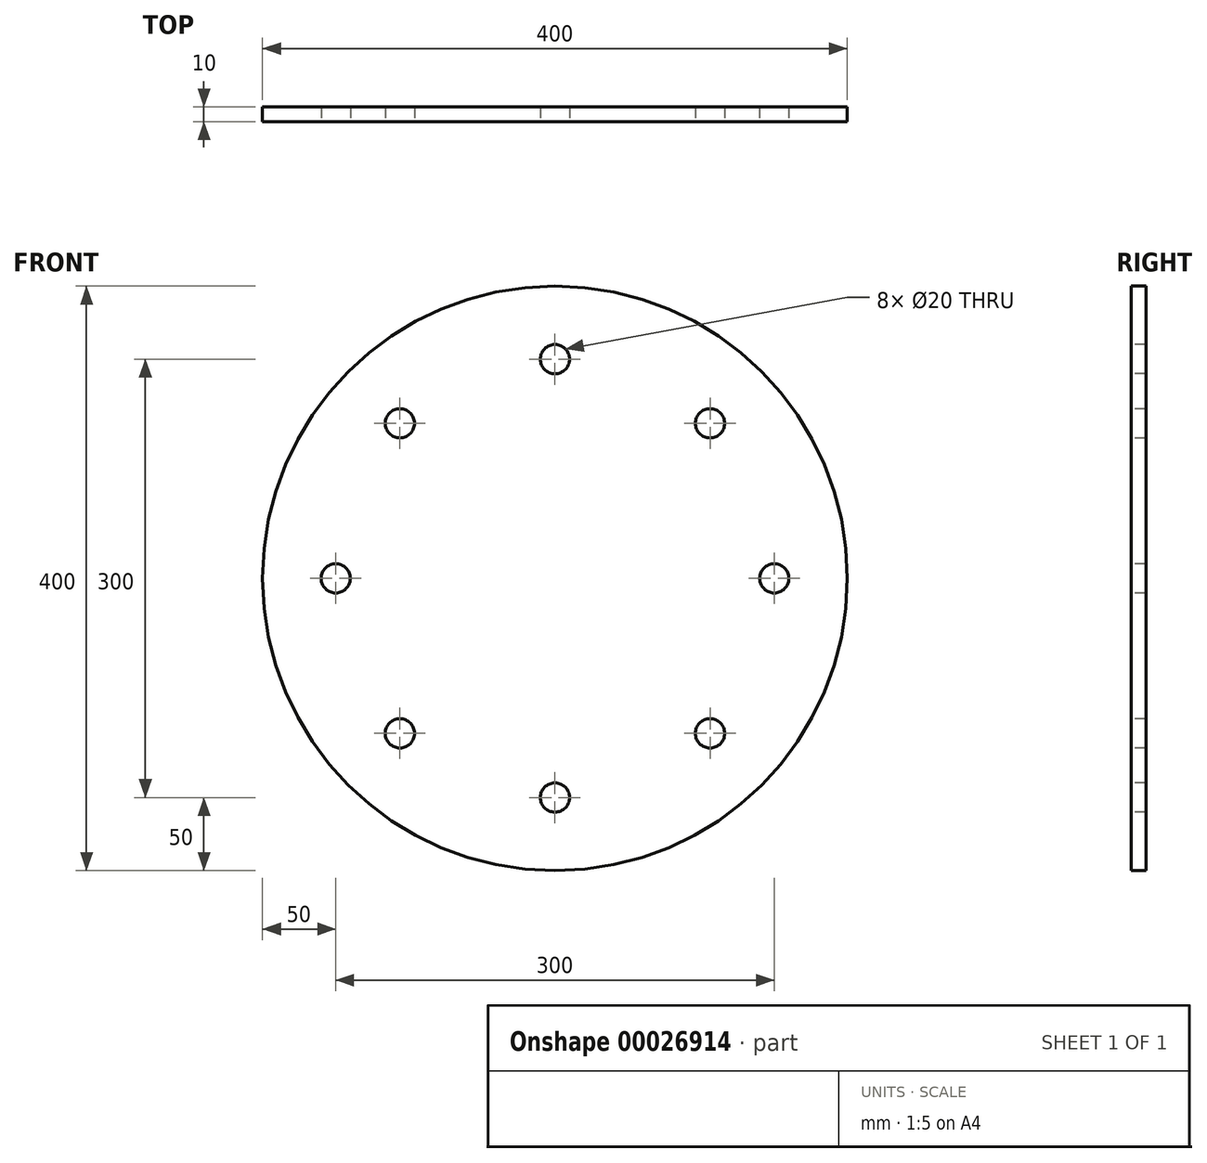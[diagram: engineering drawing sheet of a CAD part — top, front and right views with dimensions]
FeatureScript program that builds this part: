
annotation { "Feature Type Name" : "Feature", "Feature Type Description" : "" }
export const myFeature = defineFeature(function(context is Context, id is Id, definition is map)
    precondition{}
    {
        {
            var Q0;
            Q0=qCreatedBy(makeId("Front.planeOp"),FACE);
            var sketch = newSketch(context, id + "F0", { "sketchPlane" : qUnion([Q0])});
            skCircle(sketch, "E0", {"center": v(0, 0) * mm, "radius": 200 * mm});
            skSolve(sketch);
        }
        {
            var Q0;
            Q0=qSketchRegion(id+"F0",true);
            extrude(context, id + "F1", {"entities" : qUnion([Q0]), "depth" : 10 * mm});
        }
        {
            var Q0;
            Q0=makeQuery(id+"F1.opExtrude","CAP_FACE",FACE,{"disambiguationData":[OSD([sQuery(id+"F0.wireOp",EDGE,"E0")])],"isStart":false});
            var sketch = newSketch(context, id + "F2", { "sketchPlane" : qUnion([Q0])});
            skCircle(sketch, "E1", {"center": v(0, 150) * mm, "radius": 10 * mm});
            skCircle(sketch, "E2.1.0", {"center": v(-106.07, 106.07) * mm, "radius": 10 * mm});
            skCircle(sketch, "E2.2.0", {"center": v(-150, 0) * mm, "radius": 10 * mm});
            skCircle(sketch, "E2.3.0", {"center": v(-106.07, -106.07) * mm, "radius": 10 * mm});
            skCircle(sketch, "E2.4.0", {"center": v(0, -150) * mm, "radius": 10 * mm});
            skCircle(sketch, "E2.5.0", {"center": v(106.07, -106.07) * mm, "radius": 10 * mm});
            skCircle(sketch, "E2.6.0", {"center": v(150, 0) * mm, "radius": 10 * mm});
            skCircle(sketch, "E2.7.0", {"center": v(106.07, 106.07) * mm, "radius": 10 * mm});
            skPoint(sketch, "E2.center", {"position": v(0, 0) * mm});
            skSolve(sketch);
        }
        {
            var Q0;
            Q0=makeQuery(id+"F2.imprint","IMPRINT",FACE,{"disambiguationData":[TD([[makeQuery(id+"F2.imprint","IMPRINT",EDGE,{"derivedFrom":sQuery(id+"F2.wireOp",EDGE,"E2.1.0")}),1.0]])]});
            var Q1;
            Q1=makeQuery(id+"F2.imprint","IMPRINT",FACE,{"disambiguationData":[TD([[makeQuery(id+"F2.imprint","IMPRINT",EDGE,{"derivedFrom":sQuery(id+"F2.wireOp",EDGE,"E1")}),1.0]])]});
            var Q2;
            Q2=makeQuery(id+"F2.imprint","IMPRINT",FACE,{"disambiguationData":[TD([[makeQuery(id+"F2.imprint","IMPRINT",EDGE,{"derivedFrom":sQuery(id+"F2.wireOp",EDGE,"E2.7.0")}),1.0]])]});
            var Q3;
            Q3=makeQuery(id+"F2.imprint","IMPRINT",FACE,{"disambiguationData":[TD([[makeQuery(id+"F2.imprint","IMPRINT",EDGE,{"derivedFrom":sQuery(id+"F2.wireOp",EDGE,"E2.6.0")}),1.0]])]});
            var Q4;
            Q4=makeQuery(id+"F2.imprint","IMPRINT",FACE,{"disambiguationData":[TD([[makeQuery(id+"F2.imprint","IMPRINT",EDGE,{"derivedFrom":sQuery(id+"F2.wireOp",EDGE,"E2.5.0")}),1.0]])]});
            var Q5;
            Q5=makeQuery(id+"F2.imprint","IMPRINT",FACE,{"disambiguationData":[TD([[makeQuery(id+"F2.imprint","IMPRINT",EDGE,{"derivedFrom":sQuery(id+"F2.wireOp",EDGE,"E2.4.0")}),1.0]])]});
            var Q6;
            Q6=makeQuery(id+"F2.imprint","IMPRINT",FACE,{"disambiguationData":[TD([[makeQuery(id+"F2.imprint","IMPRINT",EDGE,{"derivedFrom":sQuery(id+"F2.wireOp",EDGE,"E2.3.0")}),1.0]])]});
            var Q7;
            Q7=makeQuery(id+"F2.imprint","IMPRINT",FACE,{"disambiguationData":[TD([[makeQuery(id+"F2.imprint","IMPRINT",EDGE,{"derivedFrom":sQuery(id+"F2.wireOp",EDGE,"E2.2.0")}),1.0]])]});
            extrude(context, id + "F3", {"entities" : qUnion([Q0, Q1, Q2, Q3, Q4, Q5, Q6, Q7]), "operationType" : NewBodyOperationType.REMOVE, "endBound" : BoundingType.THROUGH_ALL, "oppositeDirection" : true, "depth" : 25 * mm});
        }
    });
